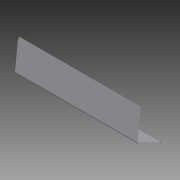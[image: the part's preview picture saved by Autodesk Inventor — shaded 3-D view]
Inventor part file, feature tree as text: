
AUTODESK INVENTOR PART (.ipt)
format: ipt  version: 2015 SP1 (Build 190203100, 203)  size: 106,496 bytes
history: native  units: in
note: dims shown in document units (in); Inventor stores cm internally (conversion verified against a paired STEP export)
features: sketch x3, extrude x2, hole x1
ambient origin geometry x8: Origin, YZ Plane, XZ Plane, XY Plane, X Axis, Y Axis, Z Axis, Center Point
bodies: Solid1 (feature_tree)
feature tree (6):
  extrude  "Extrusion1"  Depth=2.0in
  hole  "Hole1"  [1 undecoded]
  extrude  "Extrusion4"  Depth=12.0in TaperAngle=0.0deg
  sketch  "Sketch1"  dims[d0=0.0625in d1=2.0in]
  sketch  "Sketch2"  dims[d2=2.0in d3=30.0deg]
  sketch  "Sketch5"  dims[d4=0.0625in d5=12.0in d6=0.0in d7=1.125in d8=1.125in d9=5.0in d10=7.0in d11=0.25in d12=0.75in d13=0.375in d14=0.25in d15=0.5635in d16=0.25in d17=0.8108in d28=4.0in d29=1.0in d30=4.0in d31=1.0in d32=1.0in d33=1.0in d34=0.25in d35=0.0in]
note: 1 required parameter value undecoded (feature->parameter linkage not recoverable at this tier; creation-order binding heuristic only, values carry confidence <= 0.55)
